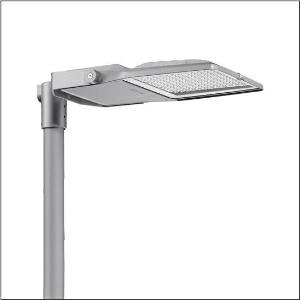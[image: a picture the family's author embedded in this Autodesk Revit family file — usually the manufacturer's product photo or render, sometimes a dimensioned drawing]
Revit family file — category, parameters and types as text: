
# Revit family: floodlight_fl_21_iq_midi___pl52_5xa7781f4d3a_7000
name_source: partatom
category: Lighting Fixtures
units: mm (PartAtom-declared; Revit-internal decimal feet)

## family parameters
Cut with Voids When Loaded = No
Host = Face
Light Source = No
Part Type = Normal
Room Calculation Point = No
Round Connector Dimension = Use Diameter
Shared = No

## types (1)
- --- (1 x LED, 37330 lm, 270.2 W, 4000K)
    Apparent Load = 270 VA
    CIE Flux Codes = 26 60 98 100 100
    Color Rendering = 70
    Color Temperature = 4000K
    Default Elevation = 1800 mm
    Description = Floodlight FL 21 iQ midi, floodlight, primary light control with lens, of PMMA, primary optical cover: protective disc, of toughened safety glass, transparent, light distribution: PL52, light emission: direct distribution, installation type: surface-mounted, LED, High Power LED, rated luminous flux: 37.330lm, luminous efficacy: 138lm/W, light colour: 740, colour temperature: 4000K, control gear: ECG iQ, control: optimised constant luminous flux control (CLO 2.0), Desk-Remote (wireless, voltage-free reading and setting of iQ features in the workshop via application-optimized NFC function/RFID function), Light-Fading, Smart-Wire, Night-Set, Lumen-Switch, Temp-Guard, Auto-Match, with terminal, 6-pole, mains connection: 220..240V, AC, 50/60Hz, start of lifetime: 270W, end of service life: 287W, reduction: 118W, luminaire housing, of diecast aluminium, powder-coated, Siteco® metallic grey (DB 702S), corrosivity category C5 mid according to DIN EN ISO 12944, sealing non-destructively replaceable, please order mast flange separately, mast bracket, of steel, galvanised, powder-coated, Siteco® metallic grey (DB 702S), protection rating (complete): IP66, insulation class (complete): insulation class II (safety insulation), certification: CE, ENEC, VDE, protection symbol: D, impact resistance: IK08, permissible operating ambient temperature: -40..+40°C, permissible operating ambient temperature for outdoor applications: -40..+50°C, standard: DIN EN 12944, LABS conformity tested according to VDMA 24364:2018-05, packaging unit: 1 piece

Light Distribution: PL52
    Height = 76 mm
    Lamp = 1 x LED
    Lamp Light Flux = 37330 lm
    Lamp Power = 270.2 W
    Lamp count = 1
    Length = 657 mm
    Luminous efficacy = 138 lm/W
    Manufacturer = Siteco
    ModVariant = No
    Model = 5XA7781F4D3A
    Number of Poles = 1
    OnlyDefault = Yes
    Power Factor = 1
    Product Name = Floodlight FL 21 iQ midi | PL52
    Product group = floodlight | pylon annexe
    ProductGroupID = 6200
    Protection Class = Protection class II
    Protection Degree = IP 66
    RLX_Detail_Level = 1
    RLX_Emergency_Light_Flux = 0 lm
    RLX_Emergency_Type = 0
    RLX_Emergency_Type_DB = No
    RlxData = <blob elided: 153785 chars, md5=91a1d6f0>
    Socket = socket
    Standby Power = 0 W
    System Light Flux = 37330 lm
    System Power = 270 W
    Type Comments = factory setting: luminous flux: 100 % | dim-lin: 254 | 620 mA
    Type Image = l_1007123.jpg
    URL = http://relux.com
    VarID = @adj_074597
    Voltage = 0 V
    Weight = 0.00 kg
    Width = 442 mm

## geometry (parser evidence)
native form markers: Blend x4, Sweep x10
no freeform markers — native parametric forms only
